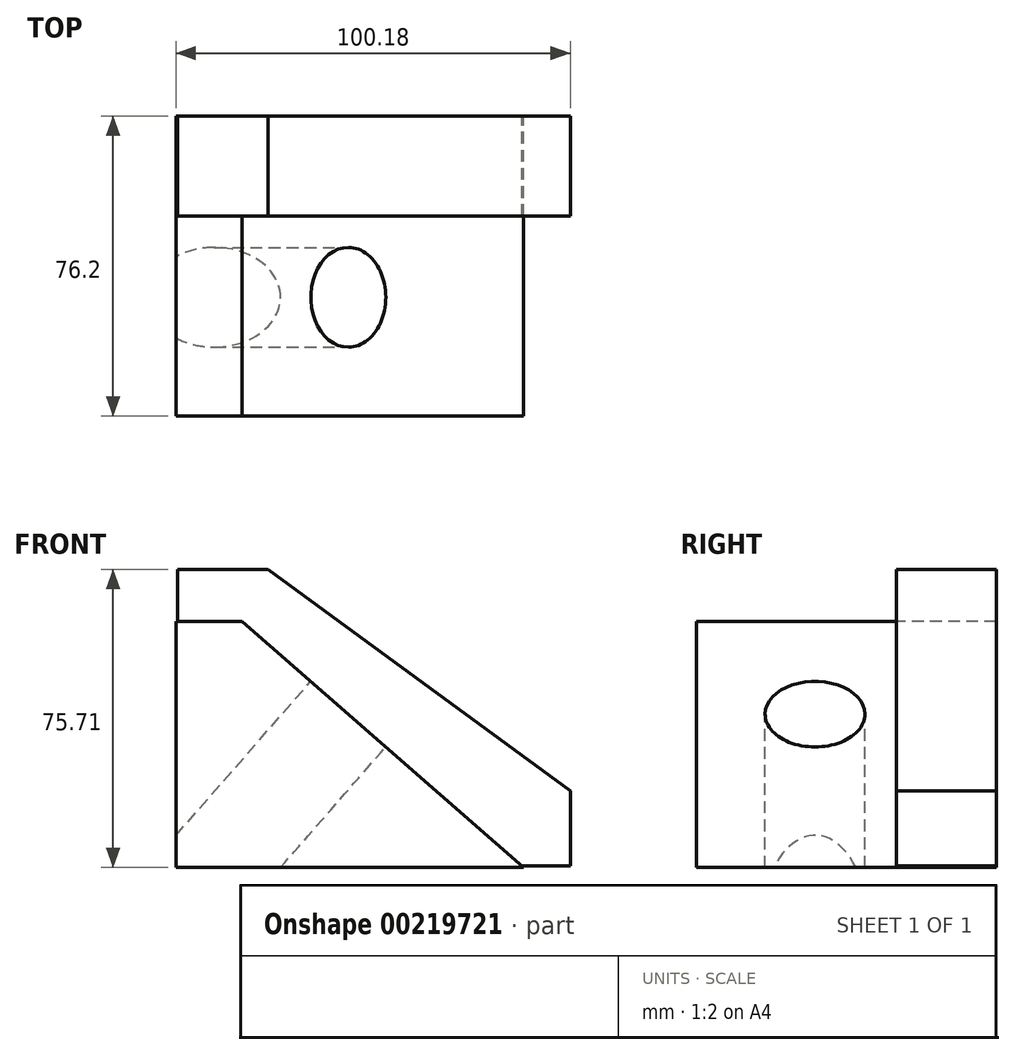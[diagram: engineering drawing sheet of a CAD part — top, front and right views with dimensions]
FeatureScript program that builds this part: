
annotation { "Feature Type Name" : "Feature", "Feature Type Description" : "" }
export const myFeature = defineFeature(function(context is Context, id is Id, definition is map)
    precondition{}
    {
        {
            var Q0;
            Q0=qCreatedBy(makeId("Front.planeOp"),FACE);
            var sketch = newSketch(context, id + "F0", { "sketchPlane" : qUnion([Q0])});
            skLineSegment(sketch, "E0.bottom", {"start": v(-44.16, 31.26) * mm, "end": v(44.16, 31.26) * mm});
            skLineSegment(sketch, "E0.top", {"start": v(-44.16, -31.26) * mm, "end": v(44.16, -31.26) * mm});
            skLineSegment(sketch, "E0.left", {"start": v(-44.16, 31.26) * mm, "end": v(-44.16, -31.26) * mm});
            skLineSegment(sketch, "E0.right", {"start": v(44.16, 31.26) * mm, "end": v(44.16, -31.26) * mm});
            skPoint(sketch, "E0.middle", {"position": v(0, 0) * mm});
            skSolve(sketch);
        }
        {
            var Q0;
            Q0=makeQuery(id+"F0.imprint","IMPRINT",FACE,{"disambiguationData":[TD([[makeQuery(id+"F0.imprint","IMPRINT",EDGE,{"derivedFrom":sQuery(id+"F0.wireOp",EDGE,"E0.bottom")}),-1.0]])]});
            extrude(context, id + "F1", {"entities" : qUnion([Q0]), "depth" : 76.2 * mm});
        }
        {
            var Q0;
            Q0=makeQuery(id+"F1.opExtrude","CAP_FACE",FACE,{"disambiguationData":[OSD([sQuery(id+"F0.wireOp",EDGE,"E0.bottom"),sQuery(id+"F0.wireOp",EDGE,"E0.top"),sQuery(id+"F0.wireOp",EDGE,"E0.left"),sQuery(id+"F0.wireOp",EDGE,"E0.right")])],"isStart":false});
            var sketch = newSketch(context, id + "F2", { "sketchPlane" : qUnion([Q0])});
            skLineSegment(sketch, "E1.0", {"start": v(-44.16, 31.26) * mm, "end": v(44.16, 31.26) * mm});
            skLineSegment(sketch, "E2.0", {"start": v(44.16, 31.26) * mm, "end": v(44.16, -31.26) * mm});
            skLineSegment(sketch, "E3", {"start": v(-27.34, 31.26) * mm, "end": v(44.16, -31.26) * mm});
            skSolve(sketch);
        }
        {
            var Q0;
            {var subQ0=sQuery(id+"F2.wireOp",EDGE,"E2.0");Q0=makeQuery(id+"F2.imprint","IMPRINT",FACE,{"disambiguationData":[TD([[makeQuery(id+"F2.imprint","IMPRINT",EDGE,{"derivedFrom":subQ0}),-1.0]])]});}
            extrude(context, id + "F3", {"entities" : qUnion([Q0]), "operationType" : NewBodyOperationType.REMOVE, "endBound" : BoundingType.THROUGH_ALL, "oppositeDirection" : true, "depth" : 76.2 * mm});
        }
        {
            var Q0;
            Q0=makeQuery(id+"F3.boolean.opBoolean","COPY",FACE,{"derivedFrom":makeQuery(id+"F3.opExtrude","SWEPT_FACE",FACE,{"disambiguationData":[OSD([sQuery(id+"F2.wireOp",EDGE,"E3")])]})});
            var sketch = newSketch(context, id + "F4", { "sketchPlane" : qUnion([Q0])});
            skCircle(sketch, "E4", {"center": v(-5.36, -46.04) * mm, "radius": 12.67 * mm});
            skSolve(sketch);
        }
        {
            var Q0;
            Q0=makeQuery(id+"F4.imprint","IMPRINT",FACE,{"disambiguationData":[TD([[makeQuery(id+"F4.imprint","IMPRINT",EDGE,{"derivedFrom":sQuery(id+"F4.wireOp",EDGE,"E4")}),1.0]])]});
            extrude(context, id + "F5", {"entities" : qUnion([Q0]), "operationType" : NewBodyOperationType.REMOVE, "endBound" : BoundingType.THROUGH_ALL, "oppositeDirection" : true, "depth" : 25.4 * mm});
        }
        {
            var Q0;
            Q0=qCreatedBy(makeId("Front.planeOp"),FACE);
            var sketch = newSketch(context, id + "F6", { "sketchPlane" : qUnion([Q0])});
            skLineSegment(sketch, "E5.bottom", {"start": v(-43.78, -30.88) * mm, "end": v(56.02, -30.88) * mm});
            skLineSegment(sketch, "E5.top", {"start": v(-43.78, 44.45) * mm, "end": v(56.02, 44.45) * mm});
            skLineSegment(sketch, "E5.left", {"start": v(-43.78, -30.88) * mm, "end": v(-43.78, 44.45) * mm});
            skLineSegment(sketch, "E5.right", {"start": v(56.02, -30.88) * mm, "end": v(56.02, 44.45) * mm});
            skSolve(sketch);
        }
        {
            var Q0;
            Q0=makeQuery(id+"F6.imprint","IMPRINT",FACE,{"disambiguationData":[TD([[makeQuery(id+"F6.imprint","IMPRINT",EDGE,{"derivedFrom":sQuery(id+"F6.wireOp",EDGE,"E5.bottom")}),1.0]])]});
            extrude(context, id + "F7", {"entities" : qUnion([Q0]), "operationType" : NewBodyOperationType.ADD, "depth" : 25.4 * mm});
        }
        {
            var Q0;
            Q0=makeQuery(id+"F7.opExtrude","CAP_FACE",FACE,{"disambiguationData":[OSD([sQuery(id+"F6.wireOp",EDGE,"E5.bottom"),sQuery(id+"F6.wireOp",EDGE,"E5.top"),sQuery(id+"F6.wireOp",EDGE,"E5.left"),sQuery(id+"F6.wireOp",EDGE,"E5.right")])],"isStart":false});
            var sketch = newSketch(context, id + "F8", { "sketchPlane" : qUnion([Q0])});
            skLineSegment(sketch, "E6.0", {"start": v(-43.78, 44.45) * mm, "end": v(56.02, 44.45) * mm});
            skLineSegment(sketch, "E7.0", {"start": v(56.02, -30.88) * mm, "end": v(56.02, 44.45) * mm});
            skLineSegment(sketch, "E8", {"start": v(-20.8, 44.45) * mm, "end": v(57.85, -13.19) * mm});
            skSolve(sketch);
        }
        {
            var Q0;
            {var subQ0=sQuery(id+"F8.wireOp",EDGE,"E7.0");var subQ1=sQuery(id+"F8.wireOp",EDGE,"E6.0");var subQ2=makeQuery(id+"F8.imprint","INTERSECT",VERTEX,{"derivedFrom":[subQ1,subQ0]});Q0=makeQuery(id+"F8.imprint","IMPRINT",FACE,{"disambiguationData":[TD([[makeQuery(id+"F8.imprint","IMPRINT",EDGE,{"disambiguationData":[TD([[subQ2,1.0]])],"derivedFrom":subQ1}),-1.0]])]});}
            extrude(context, id + "F9", {"entities" : qUnion([Q0]), "operationType" : NewBodyOperationType.REMOVE, "endBound" : BoundingType.THROUGH_ALL, "oppositeDirection" : true, "depth" : 25.4 * mm});
        }
    });
